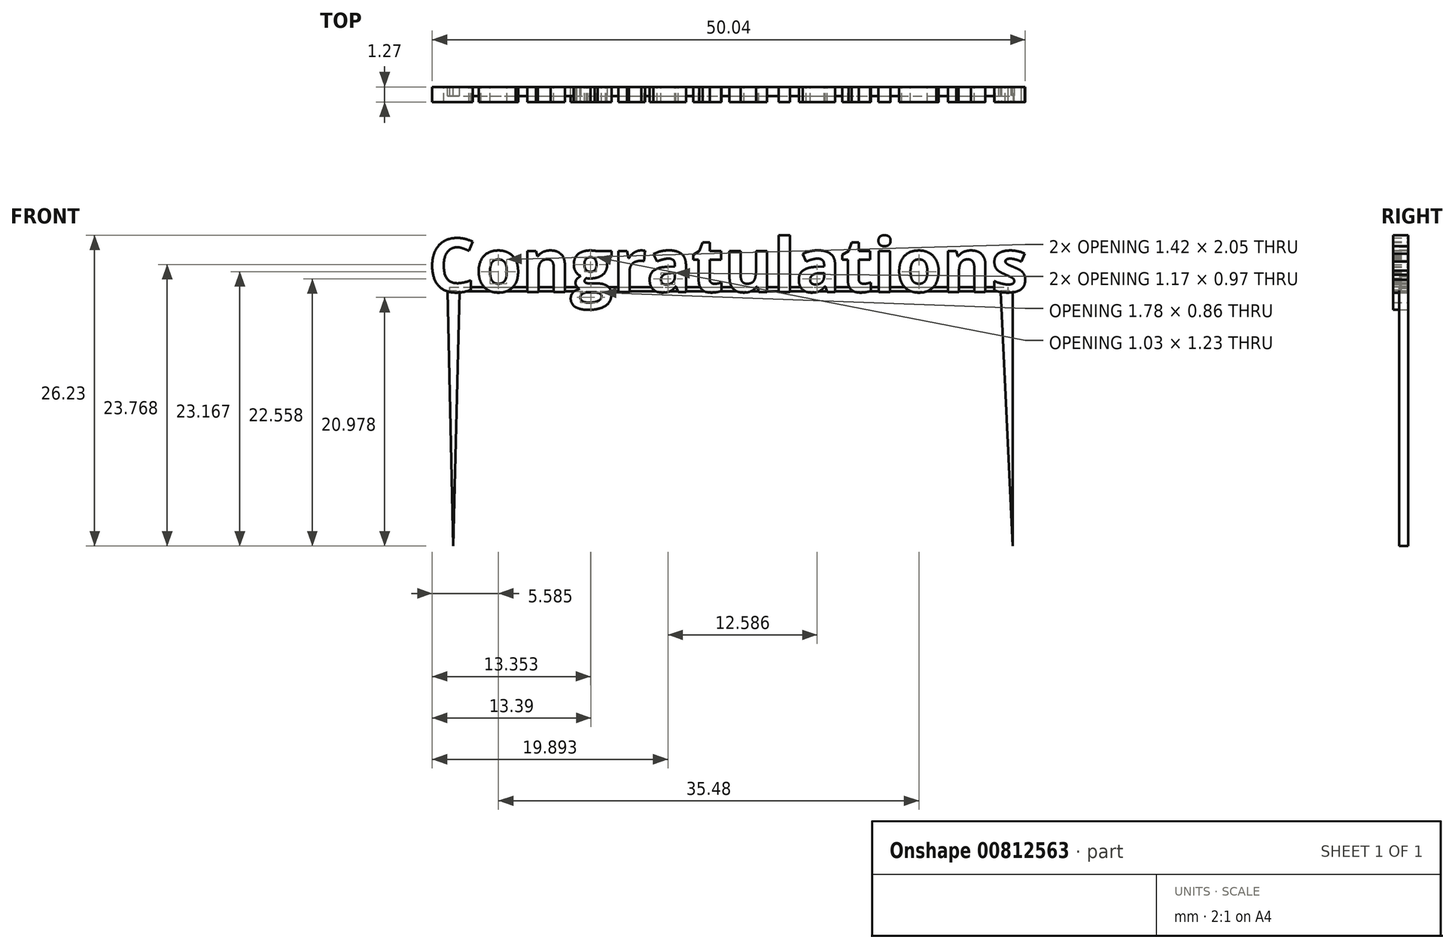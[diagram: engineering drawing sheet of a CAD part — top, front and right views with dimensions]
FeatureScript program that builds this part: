
annotation { "Feature Type Name" : "Feature", "Feature Type Description" : "" }
export const myFeature = defineFeature(function(context is Context, id is Id, definition is map)
    precondition{}
    {
        {
            var Q0;
            Q0=qCreatedBy(makeId("Front.planeOp"),FACE);
            var sketch = newSketch(context, id + "F0", { "sketchPlane" : qUnion([Q0])});
            skText(sketch, "E0", { "text": "Congratulations", "fontName": "OpenSans-Bold.ttf"});
            const initialGuessF0  = {"E0": [-0.0253, -0.00215, 1, 0, 0.00453]};
            skSetInitialGuess(sketch, initialGuessF0);
            skSolve(sketch);
        }
        {
            var Q0;
            Q0 = qSketchRegion(id + "F0", true);
            extrude(context, id + "F1", {"entities" : qUnion([Q0]), "depth" : 1.27 * mm, "offsetDistance" : 25.4 * mm});
        }
        {
            var Q0;
            Q0=qCreatedBy(makeId("Front.planeOp"),FACE);
            var sketch = newSketch(context, id + "F2", { "sketchPlane" : qUnion([Q0])});
            skLineSegment(sketch, "E1.bottom", {"start": v(-23.44, -2.1) * mm, "end": v(23.68, -2.1) * mm});
            skLineSegment(sketch, "E1.top", {"start": v(-23.44, -1.76) * mm, "end": v(23.68, -1.76) * mm});
            skLineSegment(sketch, "E1.left", {"start": v(-23.44, -2.1) * mm, "end": v(-23.44, -1.76) * mm});
            skLineSegment(sketch, "E1.right", {"start": v(23.68, -2.1) * mm, "end": v(23.68, -1.76) * mm});
            skSolve(sketch);
        }
        {
            var Q0;
            Q0=makeQuery(id+"F2.imprint","IMPRINT",FACE,{"disambiguationData":[TD([[makeQuery(id+"F2.imprint","IMPRINT",EDGE,{"derivedFrom":sQuery(id+"F2.wireOp",EDGE,"E1.bottom")}),1.0]])]});
            extrude(context, id + "F3", {"entities" : qUnion([Q0]), "depth" : 0.76 * mm, "offsetDistance" : 25.4 * mm});
        }
        {
            var Q0;
            Q0=qCreatedBy(makeId("Front.planeOp"),FACE);
            var sketch = newSketch(context, id + "F4", { "sketchPlane" : qUnion([Q0])});
            skLineSegment(sketch, "E2", {"start": v(-23.64, -2.04) * mm, "end": v(-22.61, -2.04) * mm});
            skLineSegment(sketch, "E3", {"start": v(-22.61, -2.04) * mm, "end": v(-23.16, -23.6) * mm});
            skLineSegment(sketch, "E4", {"start": v(-23.16, -23.6) * mm, "end": v(-23.64, -2.04) * mm});
            skLineSegment(sketch, "E5", {"start": v(23.04, -2.04) * mm, "end": v(24.06, -2.04) * mm});
            skLineSegment(sketch, "E6", {"start": v(24.06, -2.04) * mm, "end": v(24.06, -23.6) * mm});
            skLineSegment(sketch, "E7", {"start": v(24.06, -23.6) * mm, "end": v(23.04, -2.04) * mm});
            skSolve(sketch);
        }
        {
            var Q0;
            Q0=makeQuery(id+"F4.imprint","IMPRINT",FACE,{"disambiguationData":[TD([[makeQuery(id+"F4.imprint","IMPRINT",EDGE,{"derivedFrom":sQuery(id+"F4.wireOp",EDGE,"E2")}),-1.0]])]});
            extrude(context, id + "F5", {"entities" : qUnion([Q0]), "depth" : 0.76 * mm, "offsetDistance" : 25.4 * mm});
        }
        {
            var Q0;
            Q0 = qSketchRegion(id + "F4", true);
            extrude(context, id + "F6", {"entities" : qUnion([Q0]), "depth" : 0.76 * mm, "offsetDistance" : 25.4 * mm});
        }
    });
